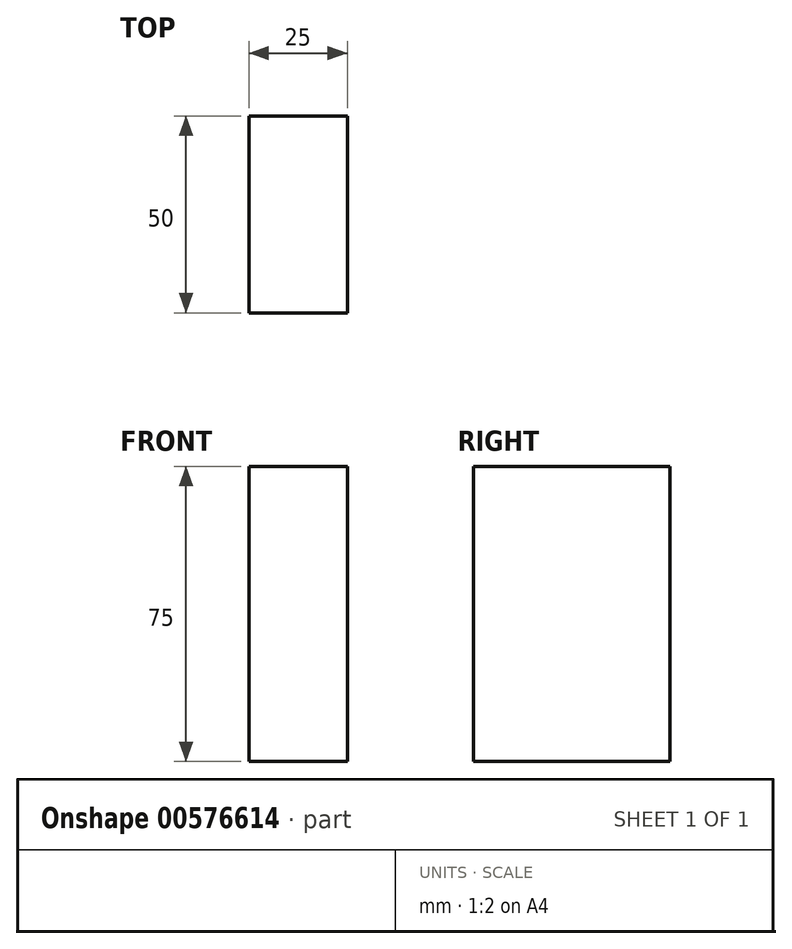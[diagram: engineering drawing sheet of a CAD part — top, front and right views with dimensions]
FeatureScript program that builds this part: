
annotation { "Feature Type Name" : "Feature", "Feature Type Description" : "" }
export const myFeature = defineFeature(function(context is Context, id is Id, definition is map)
    precondition{}
    {
        {
            var Q0;
            Q0=qCreatedBy(makeId("Top.planeOp"),FACE);
            var sketch = newSketch(context, id + "F0", { "sketchPlane" : qUnion([Q0])});
            skLineSegment(sketch, "E0.bottom", {"start": v(0, 0) * mm, "end": v(-25, 0) * mm});
            skLineSegment(sketch, "E0.top", {"start": v(0, -50) * mm, "end": v(-25, -50) * mm});
            skLineSegment(sketch, "E0.left", {"start": v(0, 0) * mm, "end": v(0, -50) * mm});
            skLineSegment(sketch, "E0.right", {"start": v(-25, 0) * mm, "end": v(-25, -50) * mm});
            skSolve(sketch);
        }
        {
            var Q0;
            Q0=makeQuery(id+"F0.imprint","IMPRINT",FACE,{"disambiguationData":[TD([[makeQuery(id+"F0.imprint","IMPRINT",EDGE,{"derivedFrom":sQuery(id+"F0.wireOp",EDGE,"E0.bottom")}),1.0]])]});
            extrude(context, id + "F1", {"entities" : qUnion([Q0]), "depth" : 75 * mm, "offsetDistance" : 25 * mm});
        }
    });
